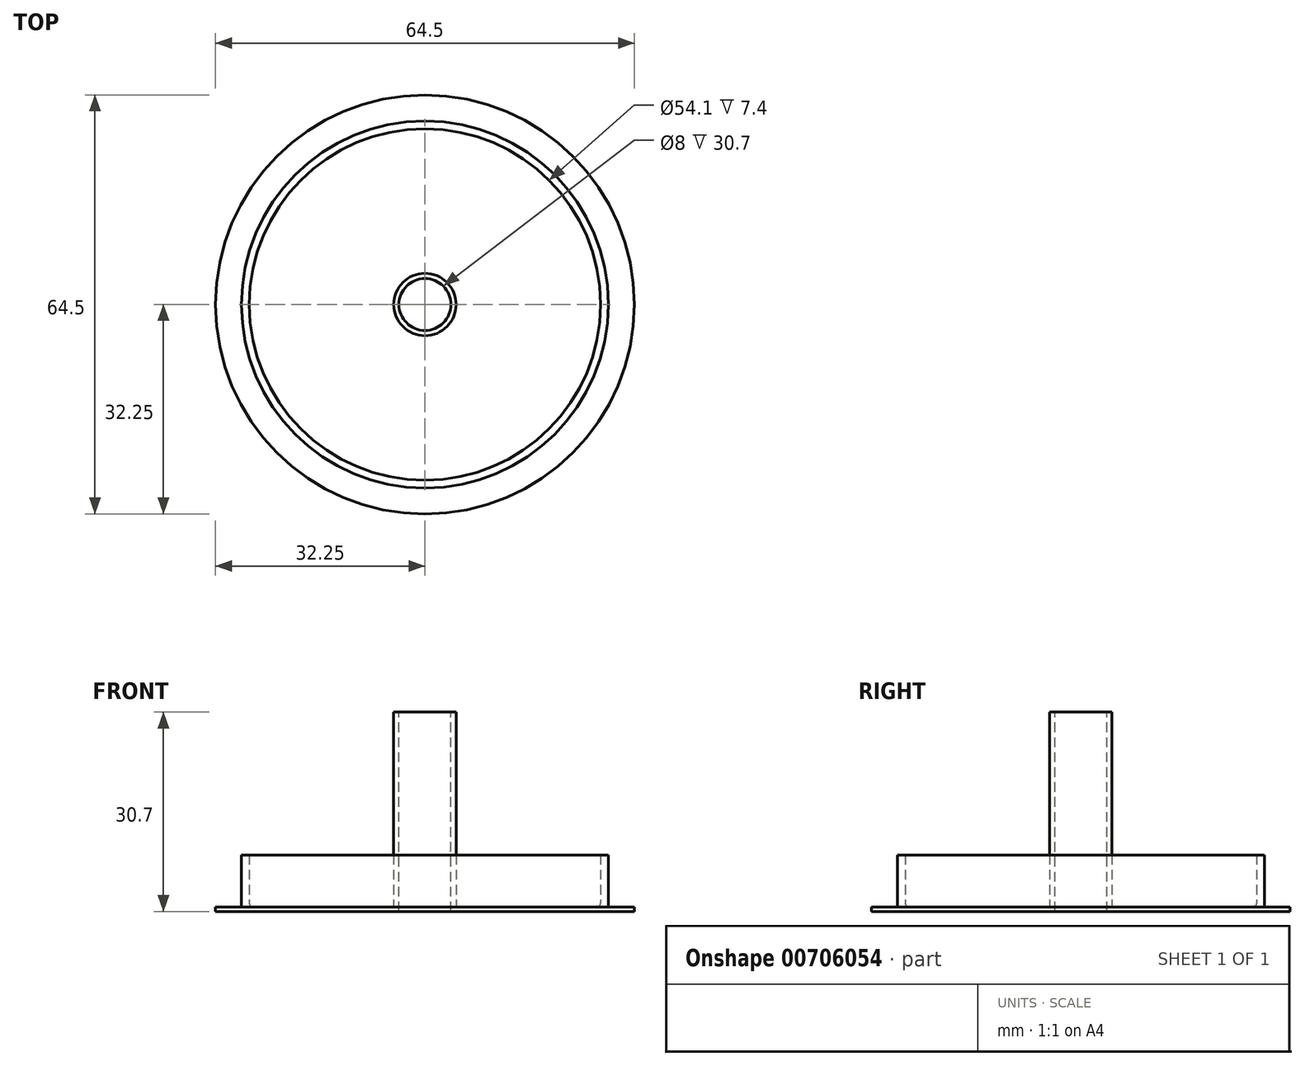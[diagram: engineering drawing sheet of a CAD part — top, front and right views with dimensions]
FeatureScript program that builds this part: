
annotation { "Feature Type Name" : "Feature", "Feature Type Description" : "" }
export const myFeature = defineFeature(function(context is Context, id is Id, definition is map)
    precondition{}
    {
        {
            var Q0;
            Q0=qCreatedBy(makeId("Top.planeOp"),FACE);
            var sketch = newSketch(context, id + "F0", { "sketchPlane" : qUnion([Q0])});
            skCircle(sketch, "E0", {"center": v(0, 0) * mm, "radius": 27.05 * mm});
            skCircle(sketch, "E1", {"center": v(0, 0) * mm, "radius": 32.25 * mm});
            skCircle(sketch, "E2", {"center": v(0, 0) * mm, "radius": 28.25 * mm});
            skCircle(sketch, "E3", {"center": v(0, 0) * mm, "radius": 4 * mm});
            skCircle(sketch, "E4", {"center": v(0, 0) * mm, "radius": 4.8 * mm});
            skSolve(sketch);
        }
        {
            var Q0;
            Q0=makeQuery(id+"F0.imprint","IMPRINT",FACE,{"disambiguationData":[TD([[makeQuery(id+"F0.imprint","IMPRINT",EDGE,{"derivedFrom":sQuery(id+"F0.wireOp",EDGE,"E0")}),-1.0]])]});
            var Q1;
            Q1=sQuery(id+"F0.wireOp",EDGE,"E2");
            extrude(context, id + "F1", {"entities" : qUnion([Q0]), "surfaceEntities" : qUnion([Q1]), "depth" : 8 * mm, "offsetDistance" : 25 * mm});
        }
        {
            var Q0;
            Q0=makeQuery(id+"F0.imprint","IMPRINT",FACE,{"disambiguationData":[TD([[makeQuery(id+"F0.imprint","IMPRINT",EDGE,{"derivedFrom":sQuery(id+"F0.wireOp",EDGE,"E1")}),1.0]])]});
            var Q1;
            Q1=makeQuery(id+"F0.imprint","IMPRINT",FACE,{"disambiguationData":[TD([[makeQuery(id+"F0.imprint","IMPRINT",EDGE,{"derivedFrom":sQuery(id+"F0.wireOp",EDGE,"E0")}),1.0]])]});
            var Q2;
            Q2=makeQuery(id+"F0.imprint","IMPRINT",FACE,{"disambiguationData":[TD([[makeQuery(id+"F0.imprint","IMPRINT",EDGE,{"derivedFrom":sQuery(id+"F0.wireOp",EDGE,"E0")}),-1.0]])]});
            var Q3;
            Q3=makeQuery(id+"F0.imprint","IMPRINT",FACE,{"disambiguationData":[TD([[makeQuery(id+"F0.imprint","IMPRINT",EDGE,{"derivedFrom":sQuery(id+"F0.wireOp",EDGE,"E3")}),-1.0]])]});
            var Q4;
            Q4=sQuery(id+"F0.wireOp",EDGE,"E1");
            extrude(context, id + "F2", {"entities" : qUnion([Q0, Q1, Q2, Q3]), "operationType" : NewBodyOperationType.ADD, "surfaceEntities" : qUnion([Q4]), "oppositeDirection" : true, "depth" : 0.7 * mm, "offsetDistance" : 25 * mm});
        }
        {
            var Q0;
            Q0=makeQuery(id+"F0.imprint","IMPRINT",FACE,{"disambiguationData":[TD([[makeQuery(id+"F0.imprint","IMPRINT",EDGE,{"derivedFrom":sQuery(id+"F0.wireOp",EDGE,"E3")}),-1.0]])]});
            extrude(context, id + "F3", {"entities" : qUnion([Q0]), "operationType" : NewBodyOperationType.ADD, "depth" : 30 * mm, "offsetDistance" : 25 * mm});
        }
        {
            var Q0;
            Q0=makeQuery(id+"F1.opExtrude","CAP_EDGE",EDGE,{"disambiguationData":[OSD([sQuery(id+"F0.wireOp",EDGE,"E2")])],"isStart":true});
            var Q1;
            Q1=makeQuery(id+"F1.opExtrude","CAP_EDGE",EDGE,{"disambiguationData":[OSD([sQuery(id+"F0.wireOp",EDGE,"E0")])],"isStart":true});
            var Q2;
            Q2=makeQuery(id+"F3.opExtrude","CAP_EDGE",EDGE,{"disambiguationData":[OSD([sQuery(id+"F0.wireOp",EDGE,"E4")])],"isStart":true});
            fillet(context, id + "F4", {"entities" : qUnion([Q0, Q1, Q2]), "radius" : 0.6 * mm, "tangentPropagation" : true, "allowEdgeOverflow" : false});
        }
    });
